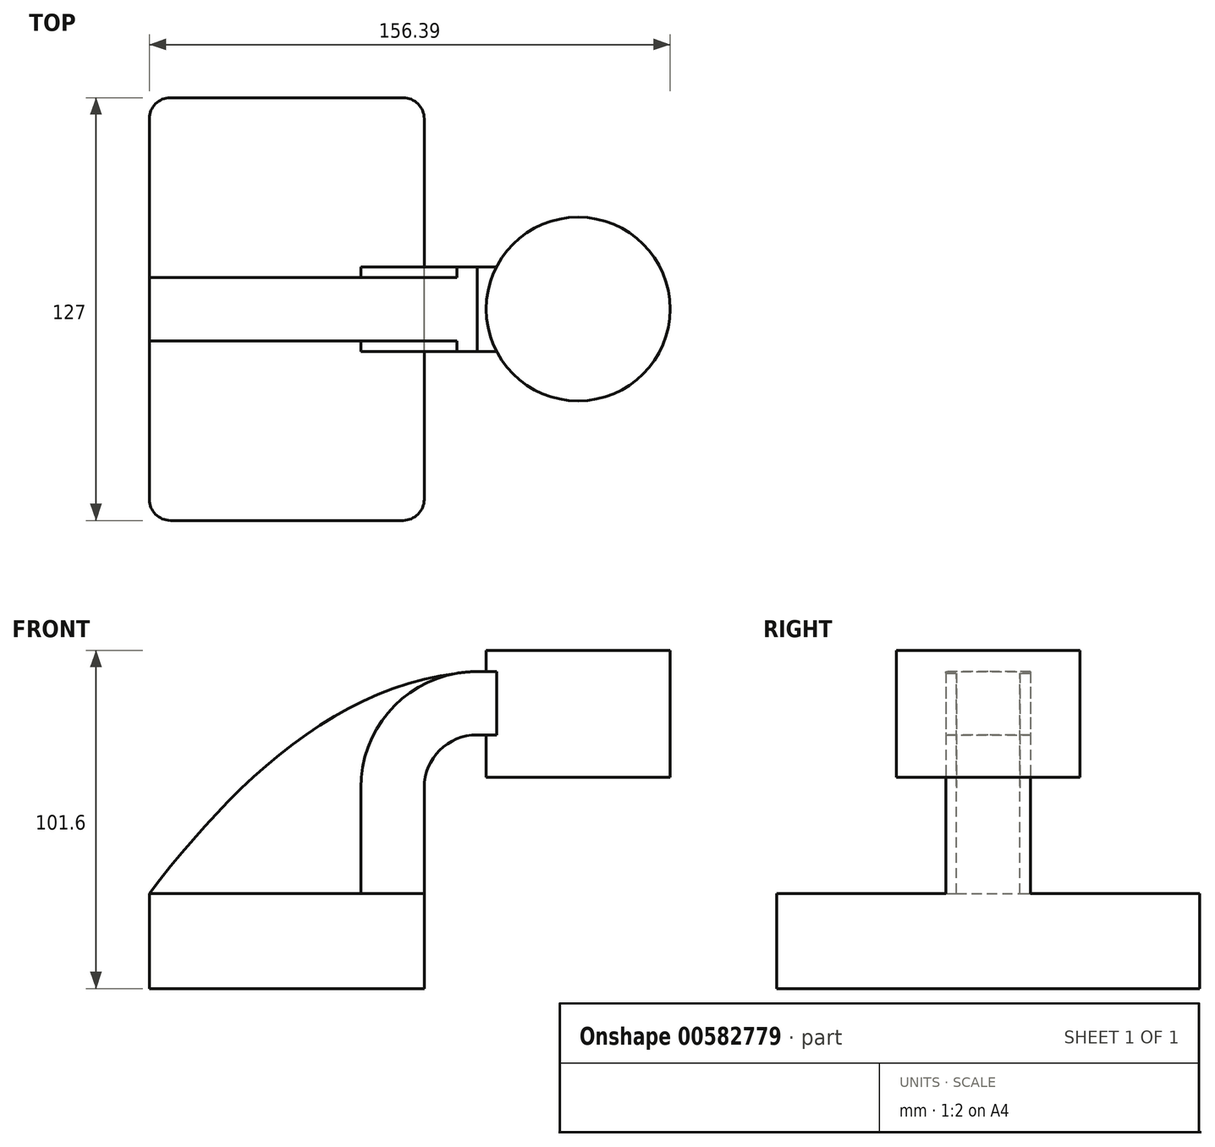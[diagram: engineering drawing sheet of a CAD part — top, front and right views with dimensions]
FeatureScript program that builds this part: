
annotation { "Feature Type Name" : "Feature", "Feature Type Description" : "" }
export const myFeature = defineFeature(function(context is Context, id is Id, definition is map)
    precondition{}
    {
        {
            var Q0;
            Q0=qCreatedBy(makeId("Front.planeOp"),FACE);
            var sketch = newSketch(context, id + "F0", { "sketchPlane" : qUnion([Q0])});
            skLineSegment(sketch, "E0.bottom", {"start": v(-41.28, 14.29) * mm, "end": v(41.27, 14.29) * mm});
            skLineSegment(sketch, "E0.top", {"start": v(-41.28, -14.29) * mm, "end": v(41.28, -14.29) * mm});
            skLineSegment(sketch, "E0.left", {"start": v(-41.28, 14.29) * mm, "end": v(-41.28, -14.29) * mm});
            skLineSegment(sketch, "E0.right", {"start": v(41.27, 14.29) * mm, "end": v(41.28, -14.29) * mm});
            skPoint(sketch, "E0.middle", {"position": v(0, 0) * mm});
            skLineSegment(sketch, "E1.bottom", {"start": v(59.92, 87.31) * mm, "end": v(115.11, 87.31) * mm});
            skLineSegment(sketch, "E1.top", {"start": v(59.92, 49.21) * mm, "end": v(115.11, 49.21) * mm});
            skLineSegment(sketch, "E1.left", {"start": v(59.92, 87.31) * mm, "end": v(59.92, 49.21) * mm});
            skLineSegment(sketch, "E1.right", {"start": v(115.11, 87.31) * mm, "end": v(115.11, 49.21) * mm});
            skPoint(sketch, "E1.middle", {"position": v(87.51, 68.26) * mm});
            skLineSegment(sketch, "E2", {"start": v(41.27, 14.29) * mm, "end": v(41.27, 46.04) * mm});
            skArc(sketch, "E3", {"start": v(41.27, 46.04) * mm, "mid": v(45.92, 57.26) * mm, "end": v(57.15, 61.91) * mm});
            skLineSegment(sketch, "E4", {"start": v(57.15, 61.91) * mm, "end": v(87.51, 61.91) * mm});
            skLineSegment(sketch, "E5.0", {"start": v(57.15, 80.96) * mm, "end": v(87.51, 80.96) * mm});
            skArc(sketch, "E5.1", {"start": v(22.22, 46.04) * mm, "mid": v(32.45, 70.73) * mm, "end": v(57.15, 80.96) * mm});
            skLineSegment(sketch, "E5.2", {"start": v(22.22, 14.29) * mm, "end": v(22.22, 46.04) * mm});
            skLineSegment(sketch, "E6", {"start": v(87.51, 49.21) * mm, "end": v(87.51, 87.31) * mm});
            skFitSpline(sketch, "E7", {"points": [v(-41.28, 14.29) * mm, v(57.15, 80.96) * mm], "startDerivative": vector(76.6, 100.16) * mm, "endDerivative": vector(122.64, 6.3) * mm});
            skSolve(sketch);
        }
        {
            var Q0;
            Q0=makeQuery(id+"F0.imprint","IMPRINT",FACE,{"disambiguationData":[TD([[makeQuery(id+"F0.imprint","IMPRINT",EDGE,{"derivedFrom":sQuery(id+"F0.wireOp",EDGE,"E0.top")}),1.0]])]});
            extrude(context, id + "F1", {"entities" : qUnion([Q0]), "endBound" : BoundingType.SYMMETRIC, "depth" : 127 * mm, "offsetDistance" : 25.4 * mm});
        }
        {
            var Q0;
            {var subQ3=sQuery(id+"F0.wireOp",EDGE,"E5.2");Q0=makeQuery(id+"F0.imprint","IMPRINT",FACE,{"disambiguationData":[TD([[makeQuery(id+"F0.imprint","IMPRINT",EDGE,{"derivedFrom":subQ3}),1.0]])]});}
            extrude(context, id + "F2", {"entities" : qUnion([Q0]), "operationType" : NewBodyOperationType.ADD, "endBound" : BoundingType.SYMMETRIC, "depth" : 19.05 * mm, "offsetDistance" : 25.4 * mm});
        }
        {
            var Q0;
            {var subQ1=sQuery(id+"F0.wireOp",EDGE,"E2");Q0=makeQuery(id+"F0.imprint","IMPRINT",FACE,{"disambiguationData":[TD([[makeQuery(id+"F0.imprint","IMPRINT",EDGE,{"derivedFrom":subQ1}),1.0]])]});}
            var Q1;
            {var subQ0=sQuery(id+"F0.wireOp",EDGE,"E5.0");var subQ1=sQuery(id+"F0.wireOp",EDGE,"E1.left");var subQ2=makeQuery(id+"F0.imprint","INTERSECT",VERTEX,{"derivedFrom":[subQ1,subQ0]});Q1=makeQuery(id+"F0.imprint","IMPRINT",FACE,{"disambiguationData":[TD([[makeQuery(id+"F0.imprint","IMPRINT",EDGE,{"disambiguationData":[TD([[subQ2,-1.0]])],"derivedFrom":subQ1}),1.0]])]});}
            extrude(context, id + "F3", {"entities" : qUnion([Q0, Q1]), "operationType" : NewBodyOperationType.ADD, "endBound" : BoundingType.SYMMETRIC, "depth" : 25.4 * mm, "offsetDistance" : 25.4 * mm});
        }
        {
            var Q0;
            {var subQ4=sQuery(id+"F0.wireOp",EDGE,"E1.right");Q0=makeQuery(id+"F0.imprint","IMPRINT",FACE,{"disambiguationData":[TD([[makeQuery(id+"F0.imprint","IMPRINT",EDGE,{"derivedFrom":subQ4}),-1.0]])]});}
            var Q1;
            Q1=sQuery(id+"F0.wireOp",EDGE,"E6");
            revolve(context, id + "F4", {"operationType" : NewBodyOperationType.ADD, "entities" : qUnion([Q0]), "axis" : qUnion([Q1]), "revolveType" : RevolveType.FULL});
        }
        {
            var Q0;
            Q0=makeQuery(id+"F1.opExtrude","CAP_EDGE",EDGE,{"disambiguationData":[OSD([sQuery(id+"F0.wireOp",EDGE,"E0.left")])],"isStart":true});
            var Q1;
            Q1=makeQuery(id+"F1.opExtrude","CAP_EDGE",EDGE,{"disambiguationData":[OSD([sQuery(id+"F0.wireOp",EDGE,"E0.right")])],"isStart":true});
            var Q2;
            Q2=makeQuery(id+"F1.opExtrude","CAP_EDGE",EDGE,{"disambiguationData":[OSD([sQuery(id+"F0.wireOp",EDGE,"E0.right")])],"isStart":false});
            var Q3;
            Q3=makeQuery(id+"F1.opExtrude","CAP_EDGE",EDGE,{"disambiguationData":[OSD([sQuery(id+"F0.wireOp",EDGE,"E0.left")])],"isStart":false});
            fillet(context, id + "F5", {"entities" : qUnion([Q0, Q1, Q2, Q3]), "radius" : 6.35 * mm, "tangentPropagation" : true, "allowEdgeOverflow" : false});
        }
    });
